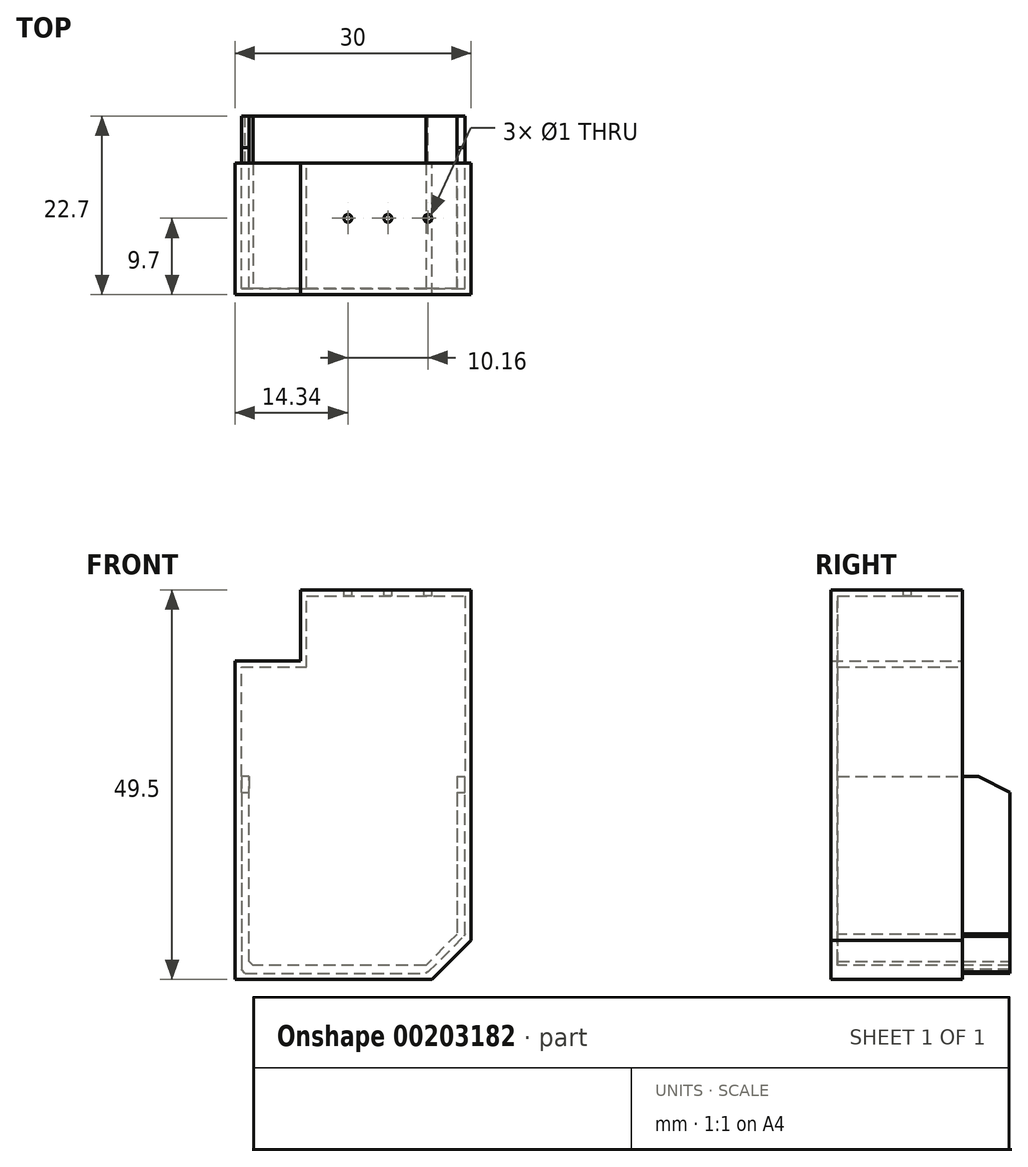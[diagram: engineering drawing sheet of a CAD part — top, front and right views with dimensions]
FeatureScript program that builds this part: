
annotation { "Feature Type Name" : "Feature", "Feature Type Description" : "" }
export const myFeature = defineFeature(function(context is Context, id is Id, definition is map)
    precondition{}
    {
        {
            assignVariable(context, id + "F0", {"name" : "epparoi", "anyValue" : 0.8});
        }
        {
            var Q0;
            Q0=qCreatedBy(makeId("Front.planeOp"),FACE);
            var sketch = newSketch(context, id + "F1", { "sketchPlane" : qUnion([Q0])});
            skLineSegment(sketch, "E0", {"start": v(0, 0) * mm, "end": v(0, 40.5) * mm});
            skLineSegment(sketch, "E1", {"start": v(0, 40.5) * mm, "end": v(8.3, 40.5) * mm});
            skLineSegment(sketch, "E2", {"start": v(8.3, 40.5) * mm, "end": v(8.3, 49.5) * mm});
            skLineSegment(sketch, "E3", {"start": v(8.3, 49.5) * mm, "end": v(30, 49.5) * mm});
            skLineSegment(sketch, "E4", {"start": v(30, 49.5) * mm, "end": v(30, 5) * mm});
            skLineSegment(sketch, "E5", {"start": v(30, 5) * mm, "end": v(25, 0) * mm});
            skLineSegment(sketch, "E6", {"start": v(25, 0) * mm, "end": v(0, 0) * mm});
            skSolve(sketch);
        }
        {
            var Q0;
            Q0=makeQuery(id+"F1.imprint","IMPRINT",FACE,{"disambiguationData":[TD([[makeQuery(id+"F1.imprint","IMPRINT",EDGE,{"derivedFrom":sQuery(id+"F1.wireOp",EDGE,"E0")}),-1.0]])]});
            extrude(context, id + "F2", {"entities" : qUnion([Q0]), "depth" : 16.7 * mm});
        }
        {
            var Q0;
            Q0=makeQuery(id+"F2.opExtrude","CAP_FACE",FACE,{"disambiguationData":[OSD([sQuery(id+"F1.wireOp",EDGE,"E0"),sQuery(id+"F1.wireOp",EDGE,"E1"),sQuery(id+"F1.wireOp",EDGE,"E2"),sQuery(id+"F1.wireOp",EDGE,"E3"),sQuery(id+"F1.wireOp",EDGE,"E4"),sQuery(id+"F1.wireOp",EDGE,"E5"),sQuery(id+"F1.wireOp",EDGE,"E6")])],"isStart":true});
            shell(context, id + "F3", {"entities" : qUnion([Q0]), "thickness" : (getVariable(context, 'epparoi')) * mm});
        }
        {
            var Q0;
            Q0=makeQuery(id+"F2.opExtrude","SWEPT_FACE",FACE,{"disambiguationData":[OSD([sQuery(id+"F1.wireOp",EDGE,"E3")])]});
            var sketch = newSketch(context, id + "F4", { "sketchPlane" : qUnion([Q0])});
            skPoint(sketch, "E7", {"position": v(24.5, -7) * mm});
            skPoint(sketch, "E8", {"position": v(19.42, -7) * mm});
            skPoint(sketch, "E9", {"position": v(14.34, -7) * mm});
            skSolve(sketch);
        }
        {
            var Q0;
            Q0=sQuery(id+"F4.wireOp",VERTEX,"E7");
            var Q1;
            Q1=sQuery(id+"F4.wireOp",VERTEX,"E8");
            var Q2;
            Q2=sQuery(id+"F4.wireOp",VERTEX,"E9");
            var Q3;
            Q3=makeQuery(id+"F2.opExtrude","SWEPT_BODY",BODY,{"disambiguationData":[OSD([sQuery(id+"F1.wireOp",EDGE,"E0"),sQuery(id+"F1.wireOp",EDGE,"E1"),sQuery(id+"F1.wireOp",EDGE,"E2"),sQuery(id+"F1.wireOp",EDGE,"E3"),sQuery(id+"F1.wireOp",EDGE,"E4"),sQuery(id+"F1.wireOp",EDGE,"E5"),sQuery(id+"F1.wireOp",EDGE,"E6")])]});
            hole(context, id + "F5", {"style" : HoleStyle.SIMPLE, "endStyle" : HoleEndStyle.BLIND, "holeDiameter" : 1 * mm, "holeDepth" : 20 * mm, "locations" : qUnion([Q0, Q1, Q2]), "scope" : qUnion([Q3])});
        }
        {
            var Q0;
            Q0=makeQuery(id+"F3.opShell","OFFSET_FACE",FACE,{"disambiguationData":[OSD([sQuery(id+"F1.wireOp",EDGE,"E0")])]});
            var sketch = newSketch(context, id + "F6", { "sketchPlane" : qUnion([Q0])});
            skLineSegment(sketch, "E10.bottom", {"start": v(-15.9, 0.8) * mm, "end": v(0, 0.8) * mm});
            skLineSegment(sketch, "E10.top", {"start": v(-15.9, 25.8) * mm, "end": v(0, 25.8) * mm});
            skLineSegment(sketch, "E10.left", {"start": v(-15.9, 0.8) * mm, "end": v(-15.9, 25.8) * mm});
            skLineSegment(sketch, "E10.right", {"start": v(0, 0.8) * mm, "end": v(0, 25.8) * mm});
            skSolve(sketch);
        }
        {
            var Q0;
            Q0=makeQuery(id+"F6.imprint","IMPRINT",FACE,{"disambiguationData":[TD([[makeQuery(id+"F6.imprint","IMPRINT",EDGE,{"derivedFrom":sQuery(id+"F6.wireOp",EDGE,"E10.bottom")}),1.0]])]});
            extrude(context, id + "F7", {"entities" : qUnion([Q0]), "operationType" : NewBodyOperationType.ADD, "depth" : 1 * mm});
        }
        {
            var Q0;
            Q0=makeQuery(id+"F3.opShell","OFFSET_FACE",FACE,{"disambiguationData":[OSD([sQuery(id+"F1.wireOp",EDGE,"E6")])]});
            extrude(context, id + "F8", {"entities" : qUnion([Q0]), "operationType" : NewBodyOperationType.ADD, "depth" : 1 * mm});
        }
        {
            var Q0;
            Q0=makeQuery(id+"F3.opShell","OFFSET_FACE",FACE,{"disambiguationData":[OSD([sQuery(id+"F1.wireOp",EDGE,"E4")])]});
            var sketch = newSketch(context, id + "F9", { "sketchPlane" : qUnion([Q0])});
            skLineSegment(sketch, "E11.bottom", {"start": v(15.9, 5.33) * mm, "end": v(0, 5.33) * mm});
            skLineSegment(sketch, "E11.top", {"start": v(15.9, 25.8) * mm, "end": v(0, 25.8) * mm});
            skLineSegment(sketch, "E11.left", {"start": v(15.9, 5.33) * mm, "end": v(15.9, 25.8) * mm});
            skLineSegment(sketch, "E11.right", {"start": v(0, 5.33) * mm, "end": v(0, 25.8) * mm});
            skSolve(sketch);
        }
        {
            var Q0;
            Q0=qSketchRegion(id+"F9",true);
            extrude(context, id + "F10", {"entities" : qUnion([Q0]), "operationType" : NewBodyOperationType.ADD, "depth" : 1 * mm});
        }
        {
            var Q0;
            Q0=makeQuery(id+"F3.opShell","OFFSET_FACE",FACE,{"disambiguationData":[OSD([sQuery(id+"F1.wireOp",EDGE,"E5")])]});
            extrude(context, id + "F11", {"entities" : qUnion([Q0]), "operationType" : NewBodyOperationType.ADD, "depth" : 1 * mm});
        }
        {
            var Q0;
            {var subQ0=sQuery(id+"F1.wireOp",EDGE,"E5");var subQ1=sQuery(id+"F1.wireOp",EDGE,"E6");Q0=makeQuery(id+"F11.boolean.opBoolean","MERGE",FACE,{"derivedFrom":[makeQuery(id+"F10.boolean.opBoolean","MERGE",FACE,{"derivedFrom":[makeQuery(id+"F8.boolean.opBoolean","MERGE",FACE,{"derivedFrom":[makeQuery(id+"F7.boolean.opBoolean","MERGE",FACE,{"derivedFrom":[makeQuery(id+"F2.opExtrude","CAP_FACE",FACE,{"disambiguationData":[OSD([sQuery(id+"F1.wireOp",EDGE,"E0"),sQuery(id+"F1.wireOp",EDGE,"E1"),sQuery(id+"F1.wireOp",EDGE,"E2"),sQuery(id+"F1.wireOp",EDGE,"E3"),sQuery(id+"F1.wireOp",EDGE,"E4"),subQ0,subQ1])],"isStart":true}),makeQuery(id+"F7.opExtrude","SWEPT_FACE",FACE,{"disambiguationData":[OSD([sQuery(id+"F6.wireOp",EDGE,"E10.right")])]})]}),makeQuery(id+"F8.opExtrude","SWEPT_FACE",FACE,{"disambiguationData":[OSD([subQ1]),TDD([makeQuery(id+"F3.opShell","OFFSET_EDGE",EDGE,{"disambiguationData":[OSD([subQ1]),TDD([makeQuery(id+"F2.opExtrude","CAP_EDGE",EDGE,{"disambiguationData":[OSD([subQ1])],"isStart":true})])]})])]})]}),makeQuery(id+"F10.opExtrude","SWEPT_FACE",FACE,{"disambiguationData":[OSD([sQuery(id+"F9.wireOp",EDGE,"E11.right")])]})]}),makeQuery(id+"F11.opExtrude","SWEPT_FACE",FACE,{"disambiguationData":[OSD([subQ0]),TDD([makeQuery(id+"F3.opShell","OFFSET_EDGE",EDGE,{"disambiguationData":[OSD([subQ0]),TDD([makeQuery(id+"F2.opExtrude","CAP_EDGE",EDGE,{"disambiguationData":[OSD([subQ0])],"isStart":true})])]})])]})]});}
            var sketch = newSketch(context, id + "F12", { "sketchPlane" : qUnion([Q0])});
            skLineSegment(sketch, "E12", {"start": v(-1.8, 25.8) * mm, "end": v(-0.8, 25.8) * mm});
            skLineSegment(sketch, "E13", {"start": v(-0.8, 25.8) * mm, "end": v(-0.8, 0.8) * mm});
            skLineSegment(sketch, "E14", {"start": v(-0.8, 0.8) * mm, "end": v(-24.39, 0.8) * mm});
            skLineSegment(sketch, "E15", {"start": v(-24.39, 0.8) * mm, "end": v(-29.2, 5.61) * mm});
            skLineSegment(sketch, "E16", {"start": v(-29.2, 5.61) * mm, "end": v(-29.2, 25.8) * mm});
            skLineSegment(sketch, "E17", {"start": v(-29.2, 25.8) * mm, "end": v(-28.2, 25.8) * mm});
            skLineSegment(sketch, "E18", {"start": v(-28.2, 25.8) * mm, "end": v(-28.2, 5.75) * mm});
            skLineSegment(sketch, "E19", {"start": v(-28.2, 5.75) * mm, "end": v(-24.25, 1.8) * mm});
            skLineSegment(sketch, "E20", {"start": v(-24.25, 1.8) * mm, "end": v(-1.8, 1.8) * mm});
            skLineSegment(sketch, "E21", {"start": v(-1.8, 1.8) * mm, "end": v(-1.8, 25.8) * mm});
            skSolve(sketch);
        }
        {
            var Q0;
            Q0=makeQuery(id+"F12.imprint","IMPRINT",FACE,{"disambiguationData":[TD([[makeQuery(id+"F12.imprint","IMPRINT",EDGE,{"derivedFrom":sQuery(id+"F12.wireOp",EDGE,"E12")}),-1.0]])]});
            extrude(context, id + "F13", {"entities" : qUnion([Q0]), "operationType" : NewBodyOperationType.ADD, "depth" : 6 * mm});
        }
        {
            var Q0;
            Q0=makeQuery(id+"F13.opExtrude","SWEPT_EDGE",EDGE,{"disambiguationData":[OSD([sQuery(id+"F12.wireOp",EDGE,"E15"),sQuery(id+"F12.wireOp",EDGE,"E16")])]});
            var Q1;
            Q1=makeQuery(id+"F13.opExtrude","SWEPT_EDGE",EDGE,{"disambiguationData":[OSD([sQuery(id+"F12.wireOp",EDGE,"E14"),sQuery(id+"F12.wireOp",EDGE,"E15")])]});
            var Q2;
            Q2=makeQuery(id+"F13.opExtrude","SWEPT_EDGE",EDGE,{"disambiguationData":[OSD([sQuery(id+"F12.wireOp",EDGE,"E13"),sQuery(id+"F12.wireOp",EDGE,"E14")])]});
            var Q3;
            Q3=makeQuery(id+"F13.boolean.opBoolean","MERGE",EDGE,{"derivedFrom":[makeQuery(id+"F8.opExtrude","CAP_EDGE",EDGE,{"disambiguationData":[OSD([sQuery(id+"F6.wireOp",EDGE,"E10.bottom")])],"isStart":false}),makeQuery(id+"F13.opExtrude","SWEPT_EDGE",EDGE,{"disambiguationData":[OSD([sQuery(id+"F12.wireOp",EDGE,"E20"),sQuery(id+"F12.wireOp",EDGE,"E21")])]})]});
            chamfer(context, id + "F14", {"entities" : qUnion([Q0, Q1, Q2, Q3]), "width" : 0.5 * mm, "tangentPropagation" : true});
        }
        {
            var Q0;
            Q0=makeQuery(id+"F13.opExtrude","CAP_EDGE",EDGE,{"disambiguationData":[OSD([sQuery(id+"F12.wireOp",EDGE,"E17")])],"isStart":false});
            var Q1;
            Q1=makeQuery(id+"F13.opExtrude","CAP_EDGE",EDGE,{"disambiguationData":[OSD([sQuery(id+"F12.wireOp",EDGE,"E12")])],"isStart":false});
            chamfer(context, id + "F15", {"entities" : qUnion([Q0, Q1]), "chamferType" : ChamferType.TWO_OFFSETS, "width1" : 4 * mm, "oppositeDirection" : true, "width2" : 2 * mm, "tangentPropagation" : true});
        }
    });
